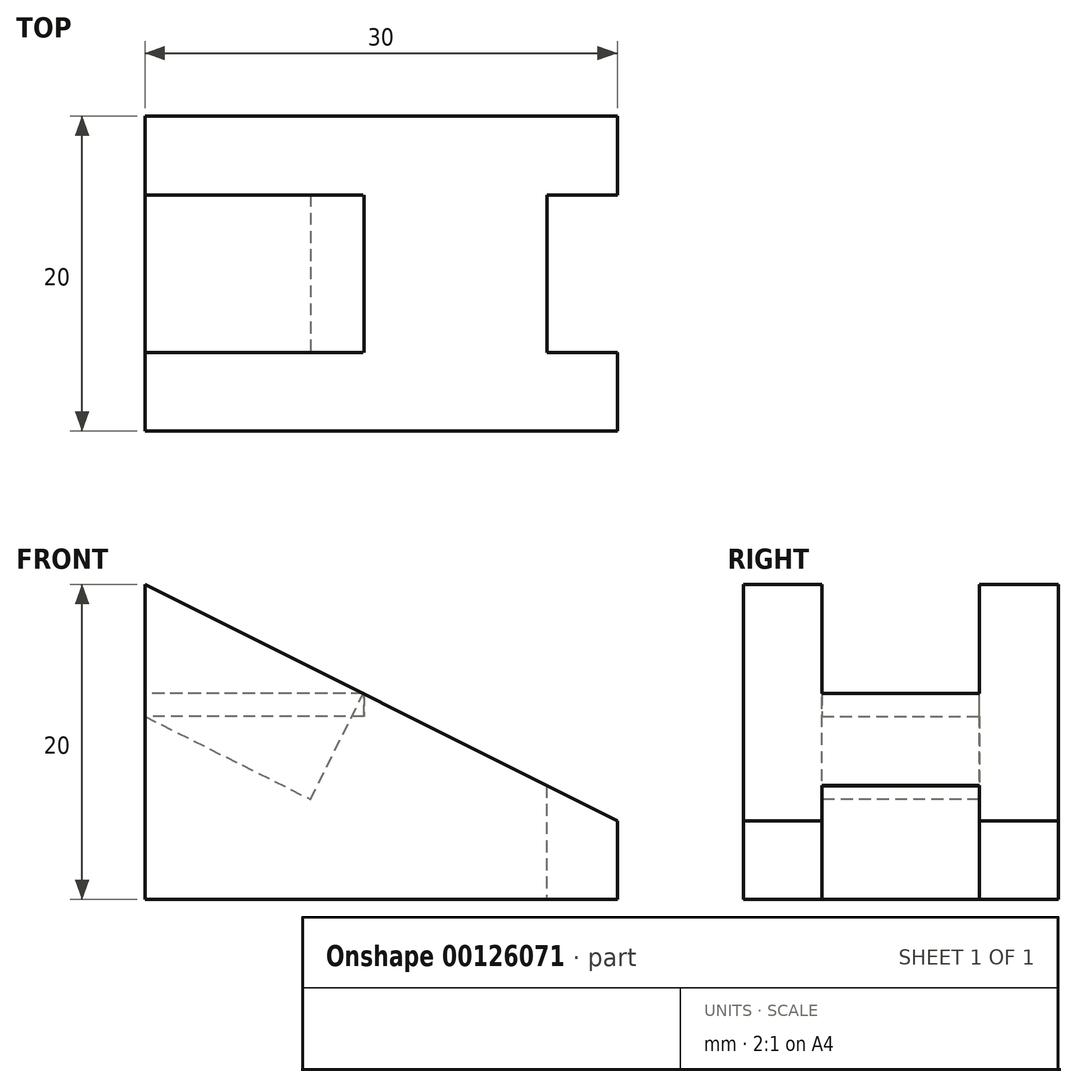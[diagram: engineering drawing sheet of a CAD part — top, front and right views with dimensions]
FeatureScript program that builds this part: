
annotation { "Feature Type Name" : "Feature", "Feature Type Description" : "" }
export const myFeature = defineFeature(function(context is Context, id is Id, definition is map)
    precondition{}
    {
        {
            var Q0;
            Q0=qCreatedBy(makeId("Front.planeOp"),FACE);
            var sketch = newSketch(context, id + "F0", { "sketchPlane" : qUnion([Q0])});
            skLineSegment(sketch, "E0", {"start": v(0, 0) * mm, "end": v(0, 20) * mm});
            skLineSegment(sketch, "E1", {"start": v(0, 20) * mm, "end": v(30, 5) * mm});
            skLineSegment(sketch, "E2", {"start": v(30, 5) * mm, "end": v(30, 0) * mm});
            skLineSegment(sketch, "E3", {"start": v(30, 0) * mm, "end": v(0, 0) * mm});
            skSolve(sketch);
        }
        {
            var Q0;
            Q0=makeQuery(id+"F0.imprint","IMPRINT",FACE,{"disambiguationData":[TD([[makeQuery(id+"F0.imprint","IMPRINT",EDGE,{"derivedFrom":sQuery(id+"F0.wireOp",EDGE,"E0")}),-1.0]])]});
            extrude(context, id + "F1", {"entities" : qUnion([Q0]), "depth" : 20 * mm});
        }
        {
            var Q0;
            Q0=makeQuery(id+"F1.opExtrude","SWEPT_FACE",FACE,{"disambiguationData":[OSD([sQuery(id+"F0.wireOp",EDGE,"E2")])]});
            var sketch = newSketch(context, id + "F2", { "sketchPlane" : qUnion([Q0])});
            skLineSegment(sketch, "E4", {"start": v(-15, 5) * mm, "end": v(-15, 0) * mm});
            skLineSegment(sketch, "E5", {"start": v(-15, 0) * mm, "end": v(-5, 0) * mm});
            skLineSegment(sketch, "E6", {"start": v(-5, 0) * mm, "end": v(-5, 5) * mm});
            skLineSegment(sketch, "E7", {"start": v(-5, 5) * mm, "end": v(-15, 5) * mm});
            skSolve(sketch);
        }
        {
            var Q0;
            Q0=makeQuery(id+"F2.imprint","IMPRINT",FACE,{"disambiguationData":[TD([[makeQuery(id+"F2.imprint","IMPRINT",EDGE,{"derivedFrom":sQuery(id+"F2.wireOp",EDGE,"E4")}),1.0]])]});
            extrude(context, id + "F3", {"entities" : qUnion([Q0]), "operationType" : NewBodyOperationType.REMOVE, "oppositeDirection" : true, "depth" : 5 * mm});
        }
        {
            var Q0;
            Q0=makeQuery(id+"F1.opExtrude","SWEPT_FACE",FACE,{"disambiguationData":[OSD([sQuery(id+"F0.wireOp",EDGE,"E1")])]});
            var sketch = newSketch(context, id + "F4", { "sketchPlane" : qUnion([Q0])});
            skLineSegment(sketch, "E8", {"start": v(24.6, -5) * mm, "end": v(19.6, -5) * mm});
            skLineSegment(sketch, "E9", {"start": v(19.6, -5) * mm, "end": v(19.6, -15) * mm});
            skLineSegment(sketch, "E10", {"start": v(19.6, -15) * mm, "end": v(24.6, -15) * mm});
            skLineSegment(sketch, "E11", {"start": v(24.6, -15) * mm, "end": v(24.6, -5) * mm});
            skSolve(sketch);
        }
        {
            var Q0;
            Q0 = qSketchRegion(id + "F4", true);
            extrude(context, id + "F5", {"entities" : qUnion([Q0]), "operationType" : NewBodyOperationType.REMOVE, "oppositeDirection" : true, "depth" : 15 * mm});
        }
        {
            var Q0;
            Q0=makeQuery(id+"F1.opExtrude","SWEPT_FACE",FACE,{"disambiguationData":[OSD([sQuery(id+"F0.wireOp",EDGE,"E1")])]});
            var sketch = newSketch(context, id + "F6", { "sketchPlane" : qUnion([Q0])});
            skLineSegment(sketch, "E12", {"start": v(-8.94, -5) * mm, "end": v(6.56, -5) * mm});
            skLineSegment(sketch, "E13", {"start": v(6.56, -5) * mm, "end": v(6.56, -15) * mm});
            skLineSegment(sketch, "E14", {"start": v(6.56, -15) * mm, "end": v(-8.94, -15) * mm});
            skLineSegment(sketch, "E15", {"start": v(-8.94, -15) * mm, "end": v(-8.94, -5) * mm});
            skSolve(sketch);
        }
        {
            var Q0;
            Q0=makeQuery(id+"F6.imprint","IMPRINT",FACE,{"disambiguationData":[TD([[makeQuery(id+"F6.imprint","IMPRINT",EDGE,{"derivedFrom":sQuery(id+"F6.wireOp",EDGE,"E12")}),-1.0]])]});
            extrude(context, id + "F7", {"entities" : qUnion([Q0]), "operationType" : NewBodyOperationType.REMOVE, "oppositeDirection" : true, "depth" : 7.5 * mm});
        }
        {
            var Q0;
            Q0=makeQuery(id+"F1.opExtrude","SWEPT_FACE",FACE,{"disambiguationData":[OSD([sQuery(id+"F0.wireOp",EDGE,"E3")])]});
            var sketch = newSketch(context, id + "F8", { "sketchPlane" : qUnion([Q0])});
            skLineSegment(sketch, "E16", {"start": v(21.9, 15) * mm, "end": v(21.9, 5) * mm});
            skLineSegment(sketch, "E17", {"start": v(21.9, 5) * mm, "end": v(25.51, 5) * mm});
            skLineSegment(sketch, "E18", {"start": v(25.51, 5) * mm, "end": v(25.51, 15) * mm});
            skLineSegment(sketch, "E19", {"start": v(25.51, 15) * mm, "end": v(21.9, 15) * mm});
            skSolve(sketch);
        }
        {
            var Q0;
            Q0 = qSketchRegion(id + "F8", true);
            extrude(context, id + "F9", {"entities" : qUnion([Q0]), "operationType" : NewBodyOperationType.ADD, "oppositeDirection" : true, "depth" : 7.2 * mm});
        }
        {
            var Q0;
            Q0=makeQuery(id+"F1.opExtrude","SWEPT_FACE",FACE,{"disambiguationData":[OSD([sQuery(id+"F0.wireOp",EDGE,"E0")])]});
            var sketch = newSketch(context, id + "F10", { "sketchPlane" : qUnion([Q0])});
            skLineSegment(sketch, "E20", {"start": v(5, 11.61) * mm, "end": v(5, 13.08) * mm});
            skLineSegment(sketch, "E21", {"start": v(5, 13.08) * mm, "end": v(15, 13.08) * mm});
            skLineSegment(sketch, "E22", {"start": v(15, 13.08) * mm, "end": v(15, 11.61) * mm});
            skLineSegment(sketch, "E23", {"start": v(15, 11.61) * mm, "end": v(5, 11.61) * mm});
            skSolve(sketch);
        }
        {
            var Q0;
            Q0=makeQuery(id+"F10.imprint","IMPRINT",FACE,{"disambiguationData":[TD([[makeQuery(id+"F10.imprint","IMPRINT",EDGE,{"derivedFrom":sQuery(id+"F10.wireOp",EDGE,"E20")}),-1.0]])]});
            extrude(context, id + "F11", {"entities" : qUnion([Q0]), "oppositeDirection" : true, "depth" : 13.9 * mm});
        }
    });
